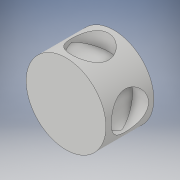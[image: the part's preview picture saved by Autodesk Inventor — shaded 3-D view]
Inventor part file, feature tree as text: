
AUTODESK INVENTOR PART (.ipt)
format: ipt  version: 2019 (Build 230136000, 136)  size: 192,000 bytes
history: native  units: mm
features: sketch x5, extrude x5, pattern_circular x1, fillet x1
ambient origin geometry x8: Origin, YZ Plane, XZ Plane, XY Plane, X Axis, Y Axis, Z Axis, Center Point
bodies: Solide1 (feature_tree)
feature tree (12):
  sketch  "Esquisse1"
  extrude  "Extrusion1"  Depth=30.0mm
  sketch  "Esquisse3"
  extrude  "Extrusion2"  Depth=3.0mm
  extrude  "Extrusion3"  Depth=7.0mm
  extrude  "Extrusion4"  Depth=3.0mm
  pattern_circular  "Réseau circulaire1"  Count=3  [1 undecoded]
  extrude  "Extrusion5"  Depth=18.0mm TaperAngle=0.0deg
  fillet  "Congé1"  Radius=14.0mm
  sketch  "Esquisse2"
  sketch  "Esquisse4"
  sketch  "Esquisse5"
note: 1 required parameter value undecoded (feature->parameter linkage not recoverable at this tier; creation-order binding heuristic only, values carry confidence <= 0.55)
